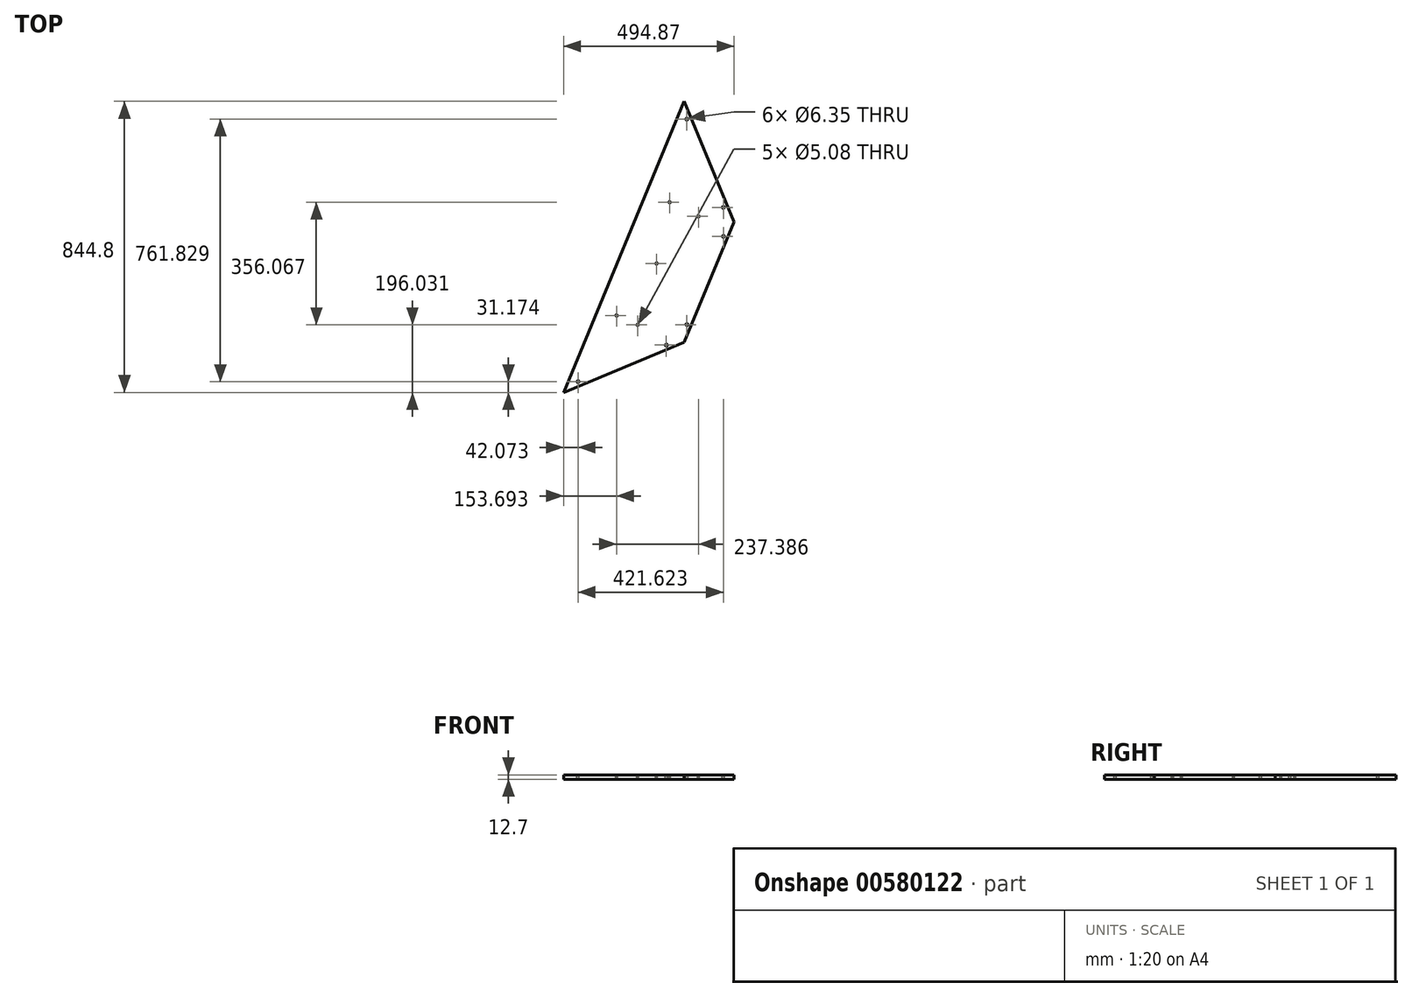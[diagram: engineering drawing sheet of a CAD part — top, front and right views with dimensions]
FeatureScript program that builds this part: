
annotation { "Feature Type Name" : "Feature", "Feature Type Description" : "" }
export const myFeature = defineFeature(function(context is Context, id is Id, definition is map)
    precondition{}
    {
        {
            var Q0;
            Q0=qCreatedBy(makeId("Top.planeOp"),FACE);
            var sketch = newSketch(context, id + "F0", { "sketchPlane" : qUnion([Q0])});
            skCircle(sketch, "E0.cCircle", {"center": v(0, 0) * mm, "radius": 494.87 * mm, "construction": true});
            skLineSegment(sketch, "E0.0", {"start": v(494.87, 0) * mm, "end": v(349.93, -349.93) * mm});
            skLineSegment(sketch, "E0.1", {"start": v(349.93, -349.93) * mm, "end": v(0, -494.87) * mm});
            skLineSegment(sketch, "E0.2", {"start": v(0, -494.87) * mm, "end": v(-349.93, -349.93) * mm});
            skLineSegment(sketch, "E0.3", {"start": v(-349.93, -349.93) * mm, "end": v(-494.87, 0) * mm});
            skLineSegment(sketch, "E0.4", {"start": v(-494.87, 0) * mm, "end": v(-349.93, 349.93) * mm});
            skLineSegment(sketch, "E0.5", {"start": v(-349.93, 349.93) * mm, "end": v(0, 494.87) * mm});
            skLineSegment(sketch, "E0.6", {"start": v(0, 494.87) * mm, "end": v(349.93, 349.93) * mm});
            skLineSegment(sketch, "E0.7", {"start": v(349.93, 349.93) * mm, "end": v(494.87, 0) * mm});
            skLineSegment(sketch, "E1", {"start": v(349.93, 349.93) * mm, "end": v(0, -494.87) * mm});
            skSolve(sketch);
        }
        {
            var Q0;
            Q0=makeQuery(id+"F0.imprint","IMPRINT",FACE,{"disambiguationData":[TD([[makeQuery(id+"F0.imprint","IMPRINT",EDGE,{"derivedFrom":sQuery(id+"F0.wireOp",EDGE,"E0.0")}),-1.0]])]});
            extrude(context, id + "F1", {"entities" : qUnion([Q0]), "depth" : 12.7 * mm, "offsetDistance" : 25.4 * mm});
        }
        {
            var Q0;
            Q0=makeQuery(id+"F1.opExtrude","CAP_FACE",FACE,{"disambiguationData":[OSD([sQuery(id+"F0.wireOp",EDGE,"E0.0"),sQuery(id+"F0.wireOp",EDGE,"E0.1"),sQuery(id+"F0.wireOp",EDGE,"E0.7"),sQuery(id+"F0.wireOp",EDGE,"E1")])],"isStart":false});
            var sketch = newSketch(context, id + "F2", { "sketchPlane" : qUnion([Q0])});
            skCircle(sketch, "E2", {"center": v(357.63, 298.13) * mm, "radius": 3.18 * mm});
            skLineSegment(sketch, "E3", {"start": v(357.63, 298.13) * mm, "end": v(354.9, 299.75) * mm});
            skLineSegment(sketch, "E4", {"start": v(357.63, 298.13) * mm, "end": v(369.37, 303) * mm});
            skCircle(sketch, "E5", {"center": v(463.7, 42.07) * mm, "radius": 3.17 * mm});
            skCircle(sketch, "E6", {"center": v(463.7, -42.07) * mm, "radius": 3.18 * mm});
            skCircle(sketch, "E7", {"center": v(357.63, -298.13) * mm, "radius": 3.17 * mm});
            skCircle(sketch, "E8", {"center": v(298.13, -357.63) * mm, "radius": 3.17 * mm});
            skCircle(sketch, "E9", {"center": v(42.07, -463.7) * mm, "radius": 3.18 * mm});
            skLineSegment(sketch, "E10", {"start": v(42.07, -463.7) * mm, "end": v(43.29, -460.76) * mm});
            skLineSegment(sketch, "E11", {"start": v(298.13, -357.63) * mm, "end": v(298.13, -354.46) * mm});
            skLineSegment(sketch, "E12", {"start": v(357.63, -298.13) * mm, "end": v(357.63, -294.96) * mm});
            skLineSegment(sketch, "E13", {"start": v(463.7, -42.07) * mm, "end": v(463.7, -38.9) * mm});
            skLineSegment(sketch, "E14", {"start": v(463.7, 45.25) * mm, "end": v(463.7, 42.07) * mm});
            skLineSegment(sketch, "E15", {"start": v(463.7, 42.07) * mm, "end": v(475.43, 46.93) * mm});
            skLineSegment(sketch, "E16", {"start": v(298.13, -357.63) * mm, "end": v(303, -369.37) * mm});
            skLineSegment(sketch, "E17", {"start": v(42.07, -463.7) * mm, "end": v(46.93, -475.43) * mm});
            skLineSegment(sketch, "E18", {"start": v(357.63, -298.13) * mm, "end": v(369.37, -303) * mm});
            skLineSegment(sketch, "E19", {"start": v(463.7, -42.07) * mm, "end": v(475.43, -46.93) * mm});
            skSolve(sketch);
        }
        {
            var Q0;
            Q0=qSketchRegion(id+"F2",true);
            extrude(context, id + "F3", {"entities" : qUnion([Q0]), "operationType" : NewBodyOperationType.REMOVE, "endBound" : BoundingType.THROUGH_ALL, "oppositeDirection" : true, "depth" : 25.4 * mm, "offsetDistance" : 25.4 * mm});
        }
        {
            var Q0;
            Q0=makeQuery(id+"F1.opExtrude","CAP_FACE",FACE,{"disambiguationData":[OSD([sQuery(id+"F0.wireOp",EDGE,"E0.0"),sQuery(id+"F0.wireOp",EDGE,"E0.1"),sQuery(id+"F0.wireOp",EDGE,"E0.7"),sQuery(id+"F0.wireOp",EDGE,"E1")])],"isStart":false});
            var sketch = newSketch(context, id + "F4", { "sketchPlane" : qUnion([Q0])});
            skPoint(sketch, "E20", {"position": v(153.7, -271.6) * mm});
            skPoint(sketch, "E21", {"position": v(307.47, 57.23) * mm});
            skPoint(sketch, "E22", {"position": v(391.08, 15.96) * mm});
            skPoint(sketch, "E23", {"position": v(214.77, -298.84) * mm});
            skPoint(sketch, "E24", {"position": v(270, -120.53) * mm});
            skSolve(sketch);
        }
        {
            var Q0;
            Q0=sQuery(id+"F4.wireOp",VERTEX,"E21");
            var Q1;
            Q1=sQuery(id+"F4.wireOp",VERTEX,"E24");
            var Q2;
            Q2=sQuery(id+"F4.wireOp",VERTEX,"E22");
            var Q3;
            Q3=sQuery(id+"F4.wireOp",VERTEX,"E23");
            var Q4;
            Q4=sQuery(id+"F4.wireOp",VERTEX,"E20");
            var Q5;
            Q5=makeQuery(id+"F1.opExtrude","SWEPT_BODY",BODY,{"disambiguationData":[OSD([sQuery(id+"F0.wireOp",EDGE,"E0.0"),sQuery(id+"F0.wireOp",EDGE,"E0.1"),sQuery(id+"F0.wireOp",EDGE,"E0.7"),sQuery(id+"F0.wireOp",EDGE,"E1")])]});
            hole(context, id + "F5", {"style" : HoleStyle.SIMPLE, "endStyle" : HoleEndStyle.THROUGH, "holeDiameter" : 5.08 * mm, "majorDiameter" : 6.35 * mm, "isTappedThrough" : true, "tappedDepth" : 12.7 * mm, "tapClearance" : 3, "locations" : qUnion([Q0, Q1, Q2, Q3, Q4]), "scope" : qUnion([Q5])});
        }
    });
